# Revit family: Sanitary_Dispensers_Slits_Paper-Dispenser_M2
name_source: partatom
category: Furniture
units: mm (PartAtom-declared; Revit-internal decimal feet)

## family parameters
Always vertical = No
Cut with Voids When Loaded = No
OmniClass Number = 23.40.20.00
OmniClass Title = General Furniture and Specialties
Room Calculation Point = No
Shared = No
Work Plane-Based = Yes

## types (1)
- Slits paper dispenser M2
    AssetType = Fixed
    BIMObjectName = Sanitary_Dispensers_Slits_Paper-Dispenser_M2
    Brand = Svedholm
    Color = Various
    Cost = 0 $
    Default Elevation = 1219 mm
    Description = A lockable paper dispenser made of powder coated steel. All colours are available upon request. Adapted for wiping paper centerfeed 245 × 190 × 190 mm. Tork M2 or equivalent. The entire SLITS collection is approved by the Swedish BYGGVARUBEDÖMNINGEN and
    DurationUnit = Year
    IfcExportAs = IfcFurnishingElementType
    IfcExportType = MIRROR
    MainColor = White
    Manufacturer = Svedholm
    ManufacturerName = Svedholm
    ManufacturerURL = https://www.svedholm.se
    Material = Metal
    MirrorMainMaterial = RAL 7021
    Model = Slits paper dispenser M2
    ModelNumber = 410.600.003
    NBSDescription = Mirrors
    NBSReference = 45-35-72/336
    Name = Slits_Paper-Dispenser_M2
    NominalDepth = 200 mm
    NominalHeight = 380 mm  [stored 1.24672 ft]
    NominalLength = 200 mm
    ProductInformation = A lockable paper dispenser made of powder coated steel. All colours are available upon request. Adapted for wiping paper centerfeed 245 × 190 × 190 mm. Tork M2 or equivalent. The entire SLITS collection is approved by the Swedish BYGGVARUBEDÖMNINGEN and
    Shape = Sculptured
    Size = 380x200 ×200 mm
    URL = https://www.svedholm.se
    Uniclass2 = Pr_40_70_22_62
    Uniclass2015Description = Paper dispensers
    Uniclass2015Reference = Pr_40_70_22_62
    Version = 1
    VersionDate = 06/07/2023
    WarrantyDurationUnit = Years

note: [stored X ft] marks values corroborated as IEEE doubles in the binary element streams (Revit-internal decimal feet)

## geometry (parser evidence)
native form markers: Sweep x5
no freeform markers — native parametric forms only
